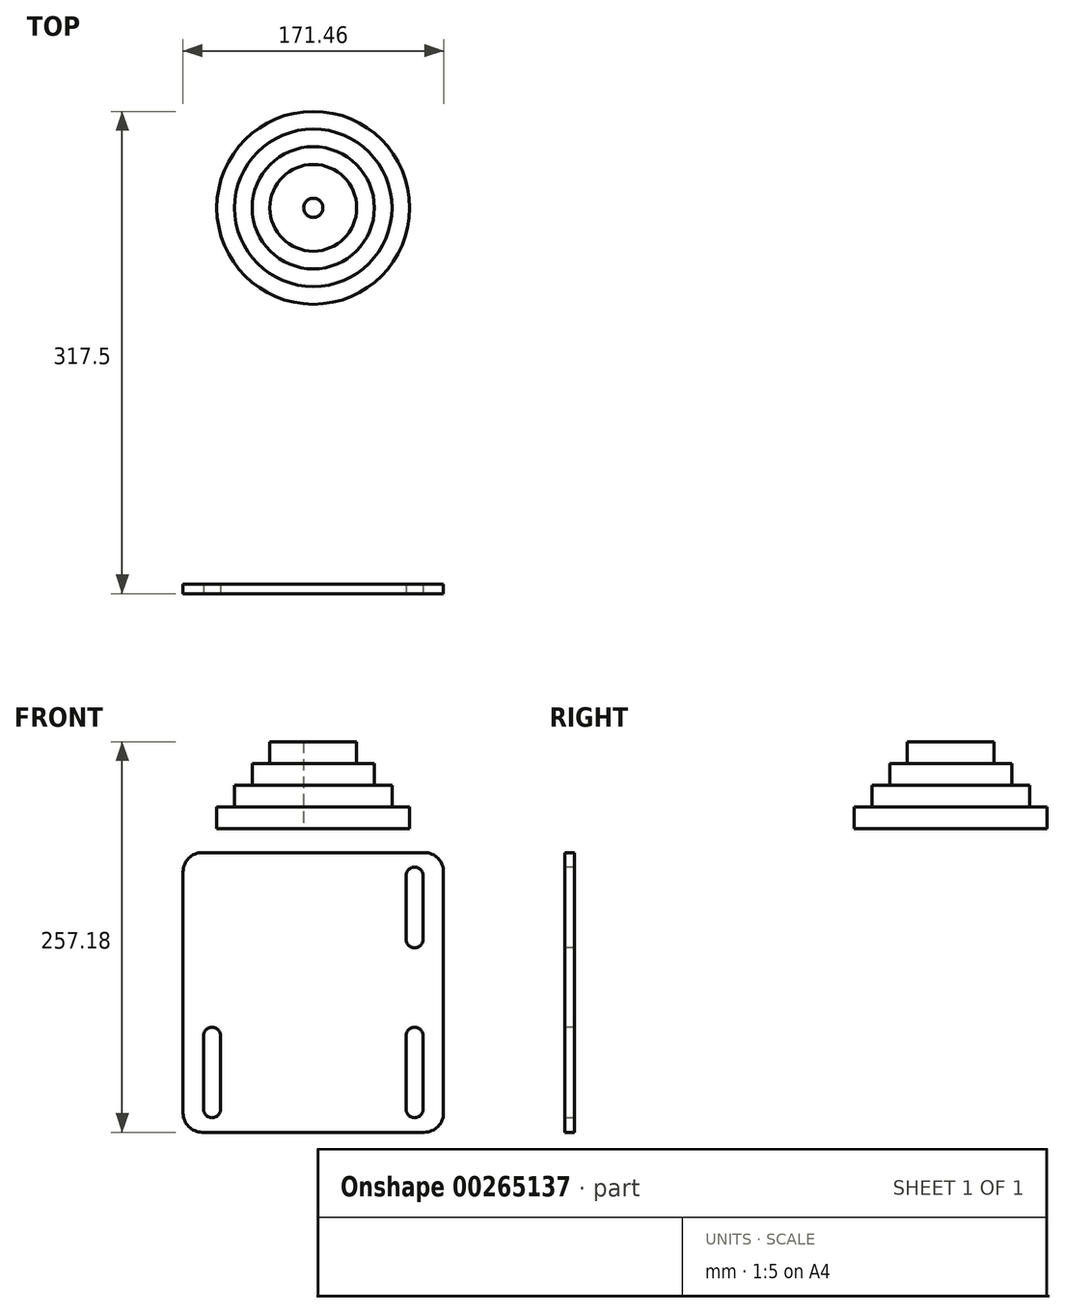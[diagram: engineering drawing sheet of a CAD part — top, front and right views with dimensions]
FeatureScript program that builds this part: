
annotation { "Feature Type Name" : "Feature", "Feature Type Description" : "" }
export const myFeature = defineFeature(function(context is Context, id is Id, definition is map)
    precondition{}
    {
        {
            var Q0;
            Q0=qCreatedBy(makeId("Front.planeOp"),FACE);
            cPlane(context, id + "F0", {"entities" : qUnion([Q0]), "cplaneType" : CPlaneType.OFFSET, "offset" : 254 * mm, "oppositeDirection" : true, "width" : 152.4 * mm, "height" : 152.4 * mm});
        }
        {
            var Q0;
            Q0=qCreatedBy(makeId("Front.planeOp"),FACE);
            var sketch = newSketch(context, id + "F1", { "sketchPlane" : qUnion([Q0])});
            skLineSegment(sketch, "E0", {"start": v(66.68, 77) * mm, "end": v(66.68, 34.92) * mm});
            skArc(sketch, "E1.0.startCap", {"start": v(61.12, 77) * mm, "mid": v(66.67, 82.55) * mm, "end": v(72.23, 77) * mm});
            skArc(sketch, "E1.0.endCap", {"start": v(72.23, 34.92) * mm, "mid": v(66.67, 29.37) * mm, "end": v(61.12, 34.92) * mm});
            skLineSegment(sketch, "E1.0.left", {"start": v(72.23, 77) * mm, "end": v(72.23, 34.92) * mm});
            skLineSegment(sketch, "E1.0.right", {"start": v(61.12, 77) * mm, "end": v(61.12, 34.92) * mm});
            skLineSegment(sketch, "E2", {"start": v(66.68, -28.58) * mm, "end": v(66.68, -77) * mm});
            skLineSegment(sketch, "E3", {"start": v(-66.68, -77) * mm, "end": v(-66.68, -28.58) * mm});
            skLineSegment(sketch, "E4", {"start": v(0, 0) * mm, "end": v(0, -38.67) * mm, "construction": true});
            skArc(sketch, "E5.0.startCap", {"start": v(61.12, -28.58) * mm, "mid": v(66.67, -23.02) * mm, "end": v(72.23, -28.58) * mm});
            skArc(sketch, "E5.0.endCap", {"start": v(72.23, -77) * mm, "mid": v(66.68, -82.55) * mm, "end": v(61.12, -77) * mm});
            skLineSegment(sketch, "E5.0.left", {"start": v(72.23, -28.58) * mm, "end": v(72.23, -77) * mm});
            skLineSegment(sketch, "E5.0.right", {"start": v(61.12, -28.58) * mm, "end": v(61.12, -77) * mm});
            skArc(sketch, "E5.1.startCap", {"start": v(-61.12, -77) * mm, "mid": v(-66.68, -82.55) * mm, "end": v(-72.23, -77) * mm});
            skArc(sketch, "E5.1.endCap", {"start": v(-72.23, -28.58) * mm, "mid": v(-66.67, -23.02) * mm, "end": v(-61.12, -28.58) * mm});
            skLineSegment(sketch, "E5.1.left", {"start": v(-72.23, -77) * mm, "end": v(-72.23, -28.58) * mm});
            skLineSegment(sketch, "E5.1.right", {"start": v(-61.12, -77) * mm, "end": v(-61.12, -28.58) * mm});
            skLineSegment(sketch, "E6.bottom", {"start": v(73.03, 92.07) * mm, "end": v(-73.02, 92.07) * mm});
            skLineSegment(sketch, "E6.top", {"start": v(73.03, -92.08) * mm, "end": v(-73.02, -92.08) * mm});
            skLineSegment(sketch, "E6.left", {"start": v(85.73, 79.38) * mm, "end": v(85.73, -79.38) * mm});
            skLineSegment(sketch, "E6.right", {"start": v(-85.73, 79.37) * mm, "end": v(-85.73, -79.38) * mm});
            skPoint(sketch, "E6.middle", {"position": v(0, 0) * mm});
            skPoint(sketch, "E7.visualSharp", {"position": v(85.73, 92.07) * mm});
            skArc(sketch, "E7.filletArc", {"start": v(85.73, 79.38) * mm, "mid": v(82, 88.36) * mm, "end": v(73.03, 92.08) * mm});
            skPoint(sketch, "E8.visualSharp", {"position": v(-85.73, 92.07) * mm});
            skArc(sketch, "E8.filletArc", {"start": v(-73.02, 92.07) * mm, "mid": v(-82, 88.36) * mm, "end": v(-85.72, 79.37) * mm});
            skPoint(sketch, "E9.visualSharp", {"position": v(-85.73, -92.08) * mm});
            skArc(sketch, "E9.filletArc", {"start": v(-85.72, -79.38) * mm, "mid": v(-82, -88.36) * mm, "end": v(-73.02, -92.08) * mm});
            skPoint(sketch, "E10.visualSharp", {"position": v(85.73, -92.08) * mm});
            skArc(sketch, "E10.filletArc", {"start": v(73.03, -92.08) * mm, "mid": v(82, -88.36) * mm, "end": v(85.73, -79.38) * mm});
            skSolve(sketch);
        }
        {
            var Q0;
            Q0 = qSketchRegion(id + "F1", true);
            extrude(context, id + "F2", {"entities" : qUnion([Q0]), "oppositeDirection" : true, "depth" : 6.35 * mm});
        }
        {
            var Q0;
            Q0=qCreatedBy(id+"F0.planeOp",FACE);
            var sketch = newSketch(context, id + "F3", { "sketchPlane" : qUnion([Q0])});
            skLineSegment(sketch, "E11", {"start": v(0, 0) * mm, "end": v(0, 144.42) * mm, "construction": true});
            skLineSegment(sketch, "E12", {"start": v(-6.35, 107.95) * mm, "end": v(-6.35, 165.1) * mm});
            skLineSegment(sketch, "E13", {"start": v(-6.35, 165.1) * mm, "end": v(-28.58, 165.1) * mm});
            skLineSegment(sketch, "E14", {"start": v(-28.58, 150.81) * mm, "end": v(-40.22, 150.81) * mm});
            skLineSegment(sketch, "E15", {"start": v(-40.22, 150.81) * mm, "end": v(-40.22, 136.53) * mm});
            skLineSegment(sketch, "E16", {"start": v(-40.22, 136.53) * mm, "end": v(-51.86, 136.53) * mm});
            skLineSegment(sketch, "E17", {"start": v(-51.86, 136.53) * mm, "end": v(-51.86, 122.24) * mm});
            skLineSegment(sketch, "E18", {"start": v(-51.86, 122.24) * mm, "end": v(-63.5, 122.24) * mm});
            skLineSegment(sketch, "E19", {"start": v(-63.5, 122.24) * mm, "end": v(-63.5, 107.95) * mm});
            skLineSegment(sketch, "E20", {"start": v(-63.5, 107.95) * mm, "end": v(-6.35, 107.95) * mm});
            skLineSegment(sketch, "E21", {"start": v(-28.58, 150.81) * mm, "end": v(-28.58, 165.1) * mm});
            skSolve(sketch);
        }
        {
            var Q0;
            Q0 = qSketchRegion(id + "F3", true);
            var Q1;
            Q1=sQuery(id+"F3.wireOp",EDGE,"E11");
            revolve(context, id + "F4", {"entities" : qUnion([Q0]), "axis" : qUnion([Q1]), "revolveType" : RevolveType.FULL});
        }
    });
